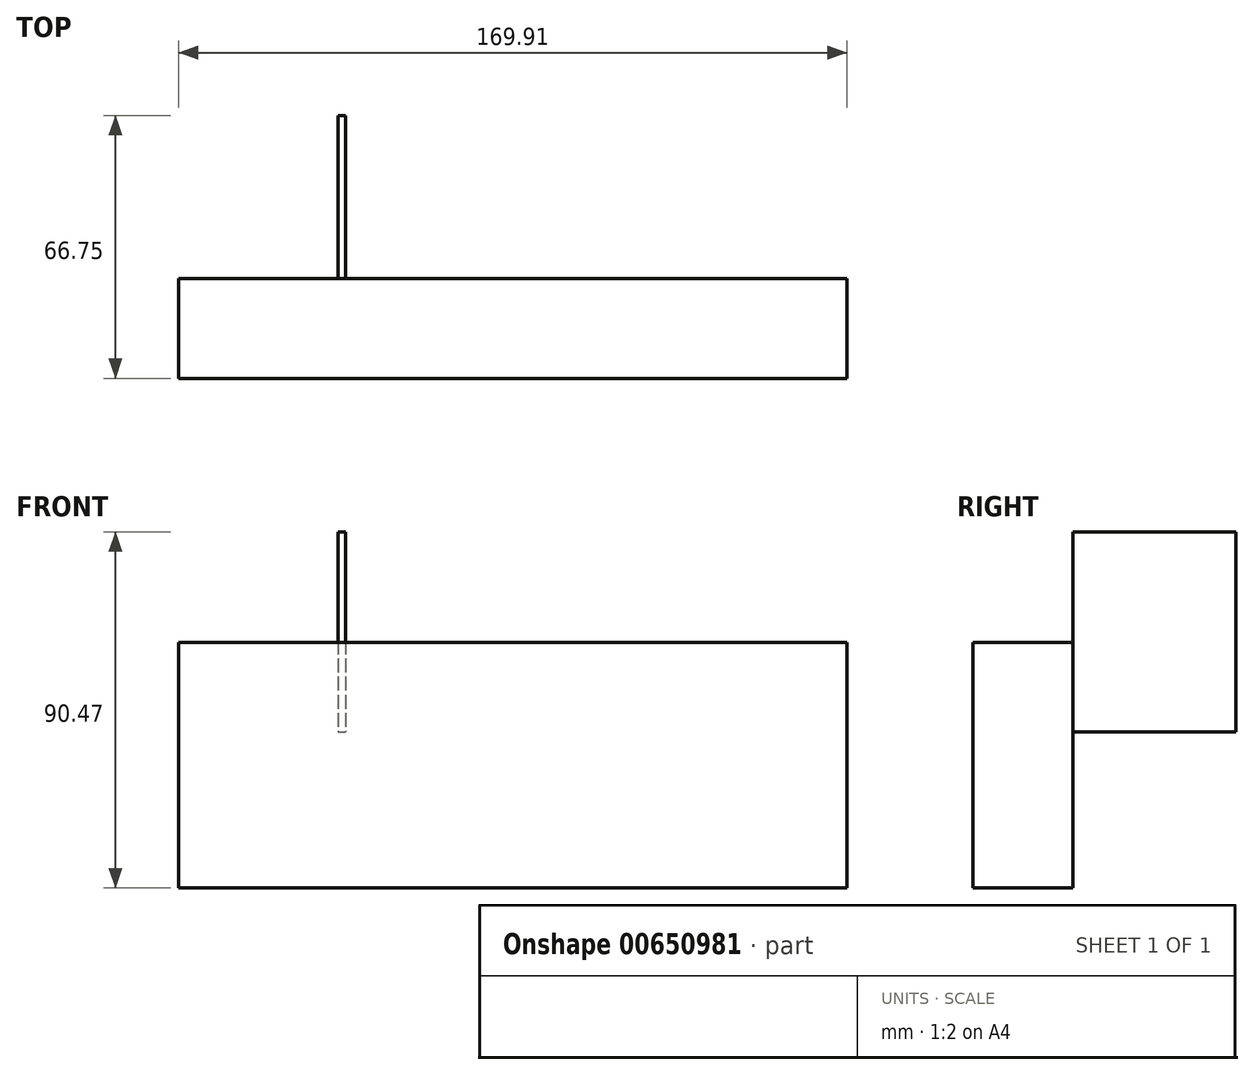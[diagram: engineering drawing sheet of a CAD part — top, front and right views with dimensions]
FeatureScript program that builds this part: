
annotation { "Feature Type Name" : "Feature", "Feature Type Description" : "" }
export const myFeature = defineFeature(function(context is Context, id is Id, definition is map)
    precondition{}
    {
        {
            var Q0;
            Q0=qCreatedBy(makeId("Top.planeOp"),FACE);
            var sketch = newSketch(context, id + "F0", { "sketchPlane" : qUnion([Q0])});
            skLineSegment(sketch, "E0.bottom", {"start": v(-133.74, -33.08) * mm, "end": v(-131.84, -33.08) * mm});
            skLineSegment(sketch, "E0.top", {"start": v(-133.74, 8.27) * mm, "end": v(-131.84, 8.27) * mm});
            skLineSegment(sketch, "E0.left", {"start": v(-133.74, -33.08) * mm, "end": v(-133.74, 8.27) * mm});
            skLineSegment(sketch, "E0.right", {"start": v(-131.84, -33.08) * mm, "end": v(-131.84, 8.27) * mm});
            skSolve(sketch);
        }
        {
            var Q0;
            Q0=makeQuery(id+"F0.imprint","IMPRINT",FACE,{"disambiguationData":[TD([[makeQuery(id+"F0.imprint","IMPRINT",EDGE,{"derivedFrom":sQuery(id+"F0.wireOp",EDGE,"E0.bottom")}),1.0]])]});
            extrude(context, id + "F1", {"entities" : qUnion([Q0]), "depth" : 50.8 * mm, "offsetDistance" : 25.4 * mm});
        }
        {
            var Q0;
            Q0=makeQuery(id+"F1.opExtrude","SWEPT_FACE",FACE,{"disambiguationData":[OSD([sQuery(id+"F0.wireOp",EDGE,"E0.right")])]});
            shell(context, id + "F2", {"entities" : qUnion([Q0]), "thickness" : 101.6 * mm});
        }
        {
            var Q0;
            Q0=makeQuery(id+"F1.opExtrude","SWEPT_FACE",FACE,{"disambiguationData":[OSD([sQuery(id+"F0.wireOp",EDGE,"E0.bottom")])]});
            var sketch = newSketch(context, id + "F3", { "sketchPlane" : qUnion([Q0])});
            skLineSegment(sketch, "E1.bottom", {"start": v(-174.28, -39.67) * mm, "end": v(-4.37, -39.67) * mm});
            skLineSegment(sketch, "E1.top", {"start": v(-174.28, 22.64) * mm, "end": v(-4.37, 22.64) * mm});
            skLineSegment(sketch, "E1.left", {"start": v(-174.28, -39.67) * mm, "end": v(-174.28, 22.64) * mm});
            skLineSegment(sketch, "E1.right", {"start": v(-4.37, -39.67) * mm, "end": v(-4.37, 22.64) * mm});
            skSolve(sketch);
        }
        {
            var Q0;
            Q0 = qSketchRegion(id + "F3", true);
            extrude(context, id + "F4", {"entities" : qUnion([Q0]), "operationType" : NewBodyOperationType.ADD, "depth" : 25.4 * mm, "offsetDistance" : 25.4 * mm});
        }
    });
